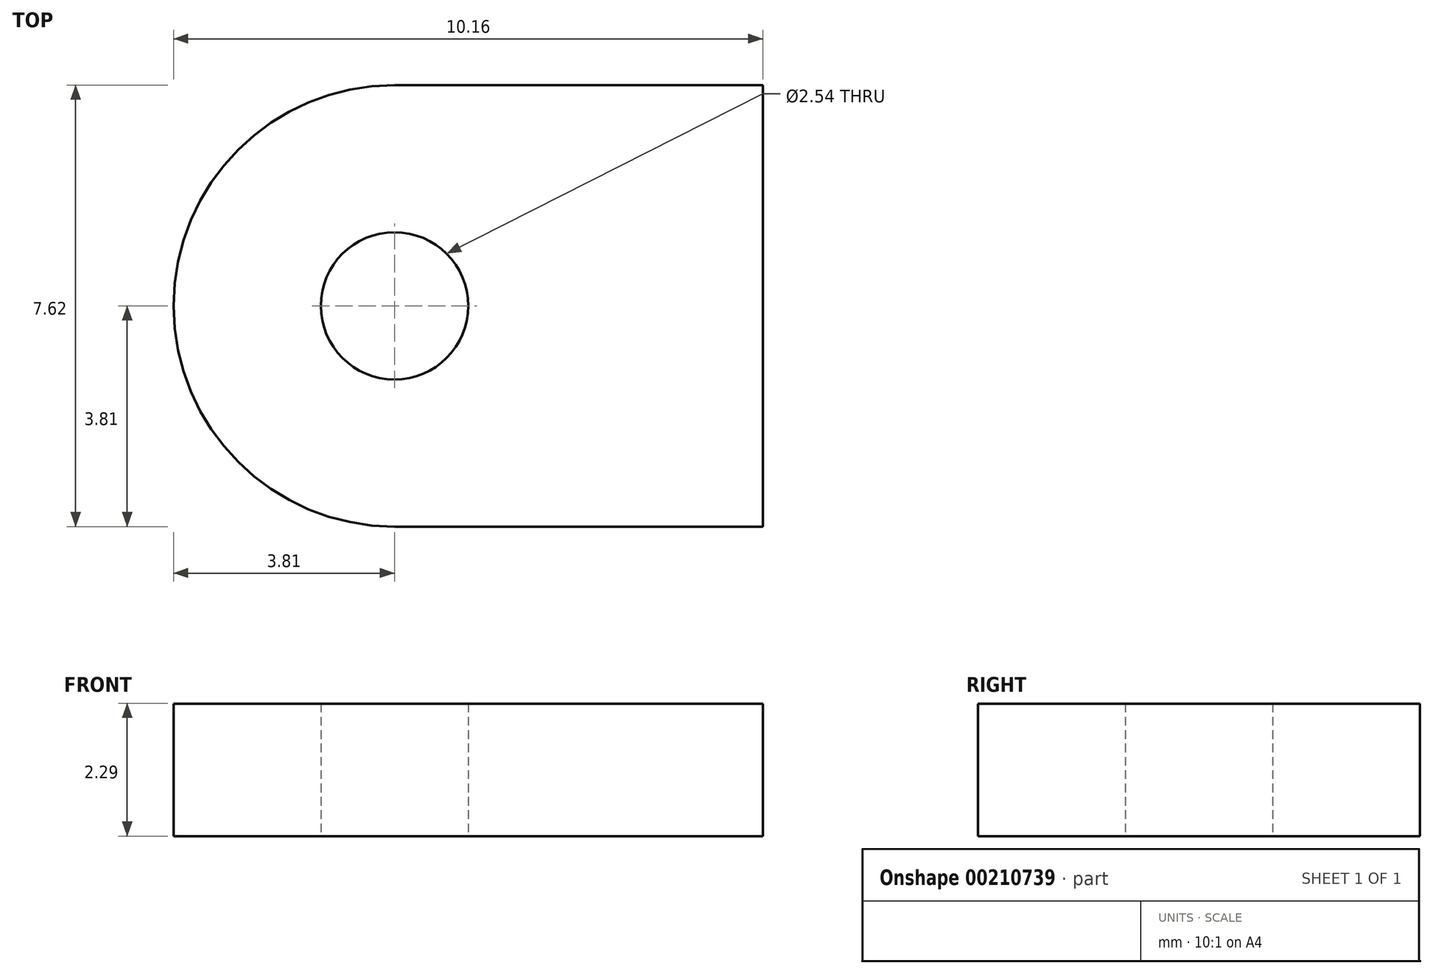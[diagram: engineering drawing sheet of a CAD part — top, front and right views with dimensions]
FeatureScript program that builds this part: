
annotation { "Feature Type Name" : "Feature", "Feature Type Description" : "" }
export const myFeature = defineFeature(function(context is Context, id is Id, definition is map)
    precondition{}
    {
        {
            var Q0;
            Q0=qCreatedBy(makeId("Top.planeOp"),FACE);
            var sketch = newSketch(context, id + "F0", { "sketchPlane" : qUnion([Q0])});
            skLineSegment(sketch, "E0.bottom", {"start": v(3.8, 0) * mm, "end": v(10.16, 0) * mm});
            skLineSegment(sketch, "E0.top", {"start": v(3.8, 7.62) * mm, "end": v(10.16, 7.62) * mm});
            skLineSegment(sketch, "E0.right", {"start": v(10.16, 0) * mm, "end": v(10.16, 7.62) * mm});
            skLineSegment(sketch, "E1", {"start": v(0, 3.81) * mm, "end": v(3.8, 3.81) * mm});
            skArc(sketch, "E2", {"start": v(3.8, 7.62) * mm, "mid": v(0, 3.81) * mm, "end": v(3.8, 0) * mm});
            skCircle(sketch, "E3", {"center": v(3.8, 3.81) * mm, "radius": 1.27 * mm});
            skPoint(sketch, "E4.orphan", {"position": v(0, 7.62) * mm});
            skPoint(sketch, "E5.orphan", {"position": v(0, 0) * mm});
            skSolve(sketch);
        }
        {
            var Q0;
            {var subQ3=sQuery(id+"F0.wireOp",EDGE,"E0.bottom");Q0=makeQuery(id+"F0.imprint","IMPRINT",FACE,{"disambiguationData":[TD([[makeQuery(id+"F0.imprint","IMPRINT",EDGE,{"derivedFrom":subQ3}),1.0]])]});}
            extrude(context, id + "F1", {"entities" : qUnion([Q0]), "depth" : 2.3 * mm});
        }
    });
